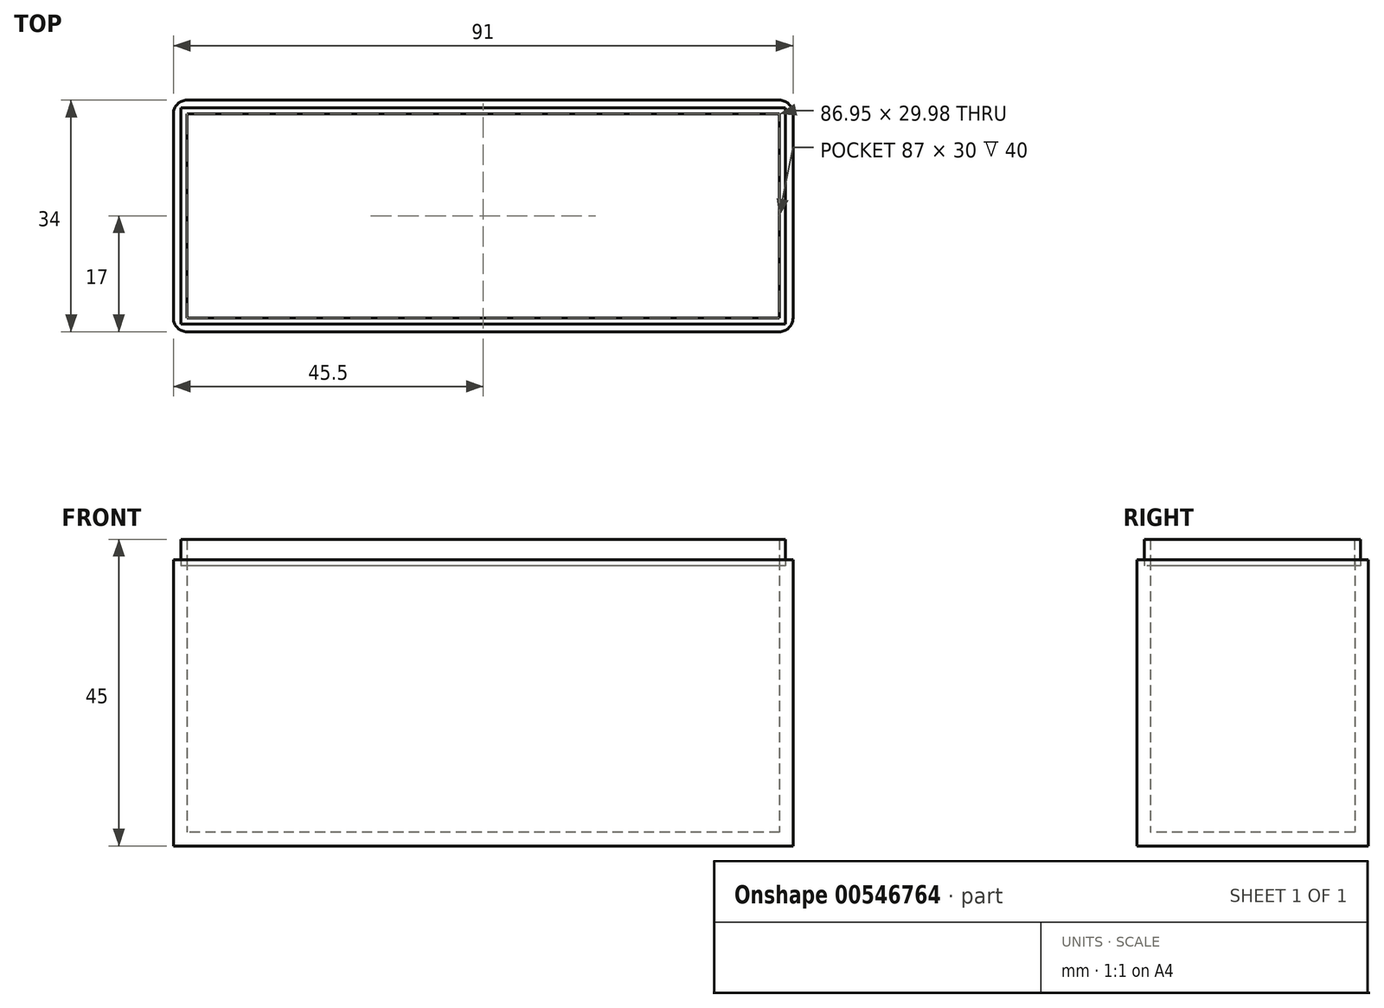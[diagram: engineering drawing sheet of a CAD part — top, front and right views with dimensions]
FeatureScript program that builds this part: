
annotation { "Feature Type Name" : "Feature", "Feature Type Description" : "" }
export const myFeature = defineFeature(function(context is Context, id is Id, definition is map)
    precondition{}
    {
        {
            var Q0;
            Q0=qCreatedBy(makeId("Top.planeOp"),FACE);
            var sketch = newSketch(context, id + "F0", { "sketchPlane" : qUnion([Q0])});
            skLineSegment(sketch, "E0.bottom", {"start": v(43.5, 15) * mm, "end": v(-43.5, 15) * mm});
            skLineSegment(sketch, "E0.top", {"start": v(43.5, -15) * mm, "end": v(-43.5, -15) * mm});
            skLineSegment(sketch, "E0.left", {"start": v(43.5, 15) * mm, "end": v(43.5, -15) * mm});
            skLineSegment(sketch, "E0.right", {"start": v(-43.5, 15) * mm, "end": v(-43.5, -15) * mm});
            skPoint(sketch, "E0.middle", {"position": v(0, 0) * mm});
            skSolve(sketch);
        }
        {
            var Q0;
            Q0=makeQuery(id+"F0.imprint","IMPRINT",FACE,{"disambiguationData":[TD([[makeQuery(id+"F0.imprint","IMPRINT",EDGE,{"derivedFrom":sQuery(id+"F0.wireOp",EDGE,"E0.bottom")}),1.0]])]});
            extrude(context, id + "F1", {"entities" : qUnion([Q0]), "depth" : 40 * mm, "offsetDistance" : 25 * mm});
        }
        {
            var Q0;
            Q0=makeQuery(id+"F1.opExtrude","CAP_FACE",FACE,{"disambiguationData":[OSD([sQuery(id+"F0.wireOp",EDGE,"E0.bottom"),sQuery(id+"F0.wireOp",EDGE,"E0.top"),sQuery(id+"F0.wireOp",EDGE,"E0.left"),sQuery(id+"F0.wireOp",EDGE,"E0.right")])],"isStart":false});
            shell(context, id + "F2", {"entities" : qUnion([Q0]), "thickness" : 2 * mm, "oppositeDirection" : true});
        }
        {
            var Q0;
            Q0=qCreatedBy(makeId("Top.planeOp"),FACE);
            cPlane(context, id + "F3", {"entities" : qUnion([Q0]), "cplaneType" : CPlaneType.OFFSET, "offset" : 40 * mm, "width" : 150 * mm, "height" : 150 * mm});
        }
        {
            var Q0;
            Q0=qCreatedBy(id+"F3.planeOp",FACE);
            var sketch = newSketch(context, id + "F4", { "sketchPlane" : qUnion([Q0])});
            skLineSegment(sketch, "E1.bottom", {"start": v(43.47, 15) * mm, "end": v(-43.47, 15) * mm});
            skLineSegment(sketch, "E1.top", {"start": v(43.47, -15) * mm, "end": v(-43.47, -15) * mm});
            skLineSegment(sketch, "E1.left", {"start": v(43.47, 15) * mm, "end": v(43.47, -15) * mm});
            skLineSegment(sketch, "E1.right", {"start": v(-43.47, 15) * mm, "end": v(-43.47, -15) * mm});
            skPoint(sketch, "E1.middle", {"position": v(0, 0) * mm});
            skSolve(sketch);
        }
        {
            var Q0;
            Q0=makeQuery(id+"F4.imprint","IMPRINT",FACE,{"disambiguationData":[TD([[makeQuery(id+"F4.imprint","IMPRINT",EDGE,{"derivedFrom":sQuery(id+"F4.wireOp",EDGE,"E1.bottom")}),1.0]])]});
            extrude(context, id + "F5", {"entities" : qUnion([Q0]), "depth" : 3 * mm, "offsetDistance" : 25 * mm});
        }
        {
            var Q0;
            Q0=makeQuery(id+"F5.opExtrude","CAP_FACE",FACE,{"disambiguationData":[OSD([sQuery(id+"F4.wireOp",EDGE,"E1.bottom"),sQuery(id+"F4.wireOp",EDGE,"E1.top"),sQuery(id+"F4.wireOp",EDGE,"E1.left"),sQuery(id+"F4.wireOp",EDGE,"E1.right")])],"isStart":false});
            shell(context, id + "F6", {"entities" : qUnion([Q0]), "thickness" : .9 * mm, "oppositeDirection" : true});
        }
        {
            var Q0;
            Q0=makeQuery(id+"F6.opShell","OFFSET_FACE",FACE,{"disambiguationData":[OSD([sQuery(id+"F4.wireOp",EDGE,"E1.bottom"),sQuery(id+"F4.wireOp",EDGE,"E1.top"),sQuery(id+"F4.wireOp",EDGE,"E1.left"),sQuery(id+"F4.wireOp",EDGE,"E1.right")])]});
            extrude(context, id + "F7", {"entities" : qUnion([Q0]), "operationType" : NewBodyOperationType.REMOVE, "oppositeDirection" : true, "depth" : 25 * mm, "offsetDistance" : 25 * mm});
        }
        {
            var Q0;
            Q0=makeQuery(id+"F1.opExtrude","SWEPT_EDGE",EDGE,{"disambiguationData":[OSD([sQuery(id+"F0.wireOp",EDGE,"E0.top"),sQuery(id+"F0.wireOp",EDGE,"E0.right")])]});
            var Q1;
            Q1=makeQuery(id+"F1.opExtrude","SWEPT_EDGE",EDGE,{"disambiguationData":[OSD([sQuery(id+"F0.wireOp",EDGE,"E0.bottom"),sQuery(id+"F0.wireOp",EDGE,"E0.right")])]});
            var Q2;
            Q2=makeQuery(id+"F1.opExtrude","SWEPT_EDGE",EDGE,{"disambiguationData":[OSD([sQuery(id+"F0.wireOp",EDGE,"E0.top"),sQuery(id+"F0.wireOp",EDGE,"E0.left")])]});
            var Q3;
            Q3=makeQuery(id+"F1.opExtrude","SWEPT_EDGE",EDGE,{"disambiguationData":[OSD([sQuery(id+"F0.wireOp",EDGE,"E0.bottom"),sQuery(id+"F0.wireOp",EDGE,"E0.left")])]});
            fillet(context, id + "F8", {"entities" : qUnion([Q0, Q1, Q2, Q3]), "radius" : 2 * mm, "tangentPropagation" : true, "allowEdgeOverflow" : false});
        }
    });
